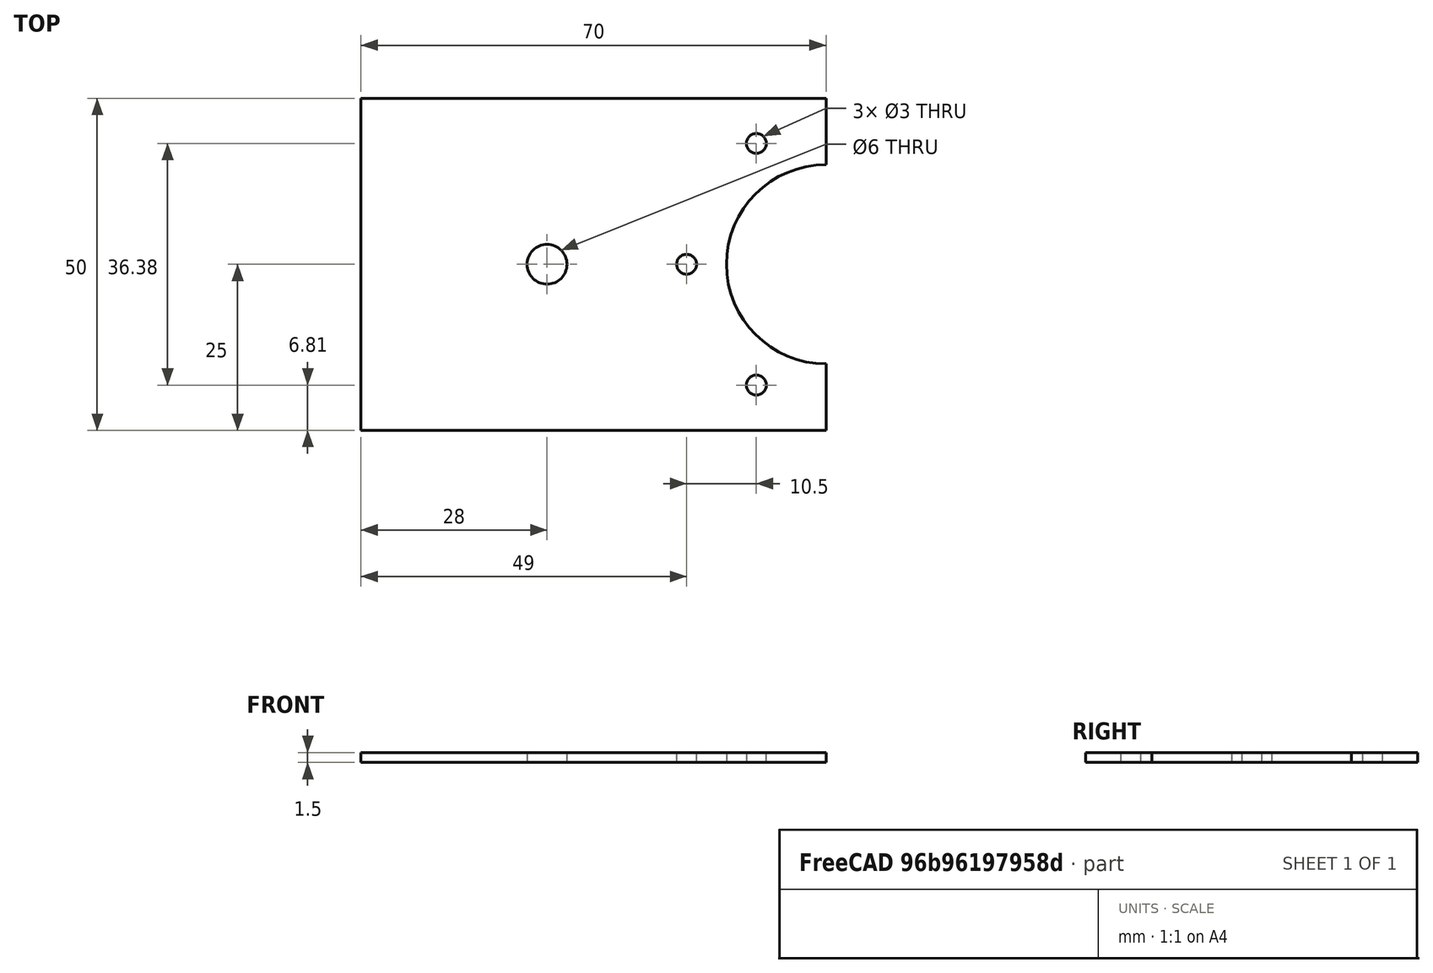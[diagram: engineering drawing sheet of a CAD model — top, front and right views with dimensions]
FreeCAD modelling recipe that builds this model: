
FCSTD DOCUMENT  (FreeCAD 0.21R33668 +26 (Git))
Label: hoja arma
License: All rights reserved
LicenseURL: https://en.wikipedia.org/wiki/All_rights_reserved
objects: TechDraw::DrawViewDimension×10, Sketcher::SketchObject×1, PartDesign::Pad×1, PartDesign::Body×1, TechDraw::DrawSVGTemplate×1, TechDraw::DrawProjGroupItem×1, TechDraw::DrawProjGroup×1, TechDraw::DrawViewAnnotation×1, TechDraw::DrawPage×1
note: 18 computed .brp shape members not serialized (recipe doc carries the construction recipe); baked Part::Feature solids carry a one-line shape summary decoded from their .brp

FEATURE [Sketcher::SketchObject] Sketch
  FullyConstrained = true
  MapMode = 5
  Support = -> [XY_Plane]
  sketch-geometry (10):
    g0: LineSegment StartX=70 StartY=0 StartZ=0 EndX=0 EndY=0 EndZ=0
    g1: LineSegment StartX=0 StartY=0 StartZ=0 EndX=0 EndY=50 EndZ=0
    g2: LineSegment StartX=0 StartY=50 StartZ=0 EndX=70 EndY=50 EndZ=0
    g3: LineSegment StartX=70 StartY=50 StartZ=0 EndX=70 EndY=40 EndZ=0
    g4: LineSegment StartX=70 StartY=0 StartZ=0 EndX=70 EndY=10 EndZ=0
    g5: ArcOfCircle CenterX=70 CenterY=25 CenterZ=0 NormalX=0 NormalY=0 NormalZ=1 AngleXU=0 Radius=15 StartAngle=1.5708 EndAngle=4.71239
    g6: Circle CenterX=28 CenterY=25 CenterZ=0 NormalX=0 NormalY=0 NormalZ=1 AngleXU=0 Radius=3
    g7: Circle CenterX=49 CenterY=25 CenterZ=0 NormalX=0 NormalY=0 NormalZ=1 AngleXU=0 Radius=1.5
    g8: Circle CenterX=59.5 CenterY=43.19 CenterZ=0 NormalX=0 NormalY=0 NormalZ=1 AngleXU=0 Radius=1.5
    g9: Circle CenterX=59.5 CenterY=6.81 CenterZ=0 NormalX=0 NormalY=0 NormalZ=1 AngleXU=0 Radius=1.5
  constraints (30):
    c: PointOnObject(g0,g-1)
    c: Coincident(g0,g-1)
    c: Coincident(g0,g1)
    c: PointOnObject(g1,g-2)
    c: Coincident(g1,g2)
    c: Horizontal(g2)
    c: DistanceY(g1,g1) = 50
    c: DistanceX(g0,g0) = 70
    c: DistanceX(g2,g2) = 70
    c: Coincident(g3,g2)
    c: Vertical(g3)
    c: Coincident(g4,g0)
    c: Vertical(g4)
    c: DistanceY(g4,g4) = 10
    c: DistanceY(g3,g3) = 10
    c: Coincident(g5,g3)
    c: Coincident(g5,g4)
    c: DistanceX(g4,g5) = 0
    c: Diameter(g6) = 6
    c: DistanceX(g0,g6) = 28
    c: DistanceY(g5,g6) = 0
    c: Diameter(g7) = 3
    c: DistanceY(g7,g5) = 0
    c: DistanceX(g7,g5) = 21
    c: DistanceX(g7,g8) = 10.5
    c: DistanceY(g7,g8) = 18.19
    c: DistanceX(g7,g9) = 10.5
    c: DistanceY(g9,g7) = 18.19
    c: Diameter(g8) = 3
    c: Diameter(g9) = 3
FEATURE [PartDesign::Pad] Pad
  Direction = (0,0,1)
  Length = 1.5
  Length2 = 10
  Profile = -> Sketch
  ReferenceAxis = -> Sketch [N_Axis]
  Type = 0
FEATURE [PartDesign::Body] Body  label="Cuerpo"
  Group = -> [Sketch,Pad]
  Origin = -> Origin
  Tip = -> Pad
FEATURE [TechDraw::DrawSVGTemplate] Template
  EditableTexts = Designed_by_Name=Enrique Gómez; Drawing_number=1; FC-Date=10/10/2023; FC-SC=2:1; FC-SH=1; FC-Title=Hoja del arma; Subtitle=Pepperoni; Weight=N/A
  Height = 210
  Orientation = 1
  Template = /snap/freecad/759/usr/share/Mod/TechDraw/Templates/A4_LandscapeTD.svg
  Width = 297
FEATURE [TechDraw::DrawProjGroupItem] ProjItem  label="Front"
  CoarseView = false
  Direction = (0,0,1)
  Focus = 100
  HardHidden = false
  IsoCount = 0
  IsoHidden = false
  IsoVisible = false
  LockPosition = true
  Perspective = false
  Rotation = 0
  RotationVector = (1,1e-06,0)
  Scale = 2
  ScaleType = 2
  ScrubCount = 0
  SeamHidden = false
  SeamVisible = false
  SmoothHidden = false
  SmoothVisible = true
  Source = -> [Body]
  Type = 0
  X = 0
  XDirection = (1,1e-06,0)
  Y = 0
FEATURE [TechDraw::DrawProjGroup] ProjGroup
  Anchor = -> ProjItem
  AutoDistribute = true
  LockPosition = false
  ProjectionType = 0
  Rotation = 0
  Scale = 2
  ScaleType = 2
  Source = -> [Body]
  Views = -> [ProjItem]
  X = 104.135
  Y = 138.929
  spacingX = 15
  spacingY = 15
FEATURE [TechDraw::DrawViewDimension] Dimension
  AngleOverride = false
  Arbitrary = false
  ArbitraryTolerances = false
  EqualTolerance = true
  ExtensionAngle = 0
  FormatSpec = %.2w
  FormatSpecOverTolerance = %+.2w
  FormatSpecUnderTolerance = %+.2w
  Inverted = false
  LineAngle = 0
  LockPosition = false
  MeasureType = 1
  OverTolerance = 0
  References2D = -> [ProjItem]
  Rotation = 0
  ScaleType = 0
  TheoreticalExact = false
  Type = 2
  UnderTolerance = 0
  X = -83.6701
  Y = -0.376252
FEATURE [TechDraw::DrawViewDimension] Dimension001
  AngleOverride = false
  Arbitrary = false
  ArbitraryTolerances = false
  EqualTolerance = true
  ExtensionAngle = 0
  FormatSpec = %.2w
  FormatSpecOverTolerance = %+.2w
  FormatSpecUnderTolerance = %+.2w
  Inverted = false
  LineAngle = 0
  LockPosition = false
  MeasureType = 1
  OverTolerance = 0
  References2D = -> [ProjItem]
  Rotation = 0
  ScaleType = 0
  TheoreticalExact = false
  Type = 1
  UnderTolerance = 0
  X = -4.80173
  Y = -64.0963
FEATURE [TechDraw::DrawViewDimension] Dimension002
  AngleOverride = false
  Arbitrary = false
  ArbitraryTolerances = false
  EqualTolerance = true
  ExtensionAngle = 0
  FormatSpec = ⌀%.2w
  FormatSpecOverTolerance = %+.2w
  FormatSpecUnderTolerance = %+.2w
  Inverted = false
  LineAngle = 0
  LockPosition = false
  MeasureType = 1
  OverTolerance = 0
  References2D = -> [ProjItem]
  Rotation = 0
  ScaleType = 0
  TheoreticalExact = false
  Type = 5
  UnderTolerance = 0
  X = -32.8764
  Y = -3.71677
FEATURE [TechDraw::DrawViewDimension] Dimension003
  AngleOverride = false
  Arbitrary = false
  ArbitraryTolerances = false
  EqualTolerance = true
  ExtensionAngle = 0
  FormatSpec = ⌀%.2w
  FormatSpecOverTolerance = %+.2w
  FormatSpecUnderTolerance = %+.2w
  Inverted = false
  LineAngle = 0
  LockPosition = false
  MeasureType = 1
  OverTolerance = 0
  References2D = -> [ProjItem]
  Rotation = 0
  ScaleType = 0
  TheoreticalExact = false
  Type = 5
  UnderTolerance = 0
  X = 4.26946
  Y = -6.57343
FEATURE [TechDraw::DrawViewDimension] Dimension004
  AngleOverride = false
  Arbitrary = false
  ArbitraryTolerances = false
  EqualTolerance = true
  ExtensionAngle = 0
  FormatSpec = R%.2w
  FormatSpecOverTolerance = %+.2w
  FormatSpecUnderTolerance = %+.2w
  Inverted = false
  LineAngle = 0
  LockPosition = false
  MeasureType = 1
  OverTolerance = 0
  References2D = -> [ProjItem]
  Rotation = 0
  ScaleType = 0
  TheoreticalExact = false
  Type = 4
  UnderTolerance = 0
  X = 54.8136
  Y = -1.79481
FEATURE [TechDraw::DrawViewDimension] Dimension005
  AngleOverride = false
  Arbitrary = false
  ArbitraryTolerances = false
  EqualTolerance = true
  ExtensionAngle = 0
  FormatSpec = %.2w
  FormatSpecOverTolerance = %+.2w
  FormatSpecUnderTolerance = %+.2w
  Inverted = false
  LineAngle = 0
  LockPosition = false
  MeasureType = 1
  OverTolerance = 0
  References2D = -> [ProjItem]
  Rotation = 0
  ScaleType = 0
  TheoreticalExact = false
  Type = 2
  UnderTolerance = 0
  X = 83.9793
  Y = -37.4718
FEATURE [TechDraw::DrawViewDimension] Dimension008
  AngleOverride = false
  Arbitrary = false
  ArbitraryTolerances = false
  EqualTolerance = true
  ExtensionAngle = 0
  FormatSpec = %.2w
  FormatSpecOverTolerance = %+.2w
  FormatSpecUnderTolerance = %+.2w
  Inverted = false
  LineAngle = 0
  LockPosition = false
  MeasureType = 1
  OverTolerance = 0
  References2D = -> [ProjItem]
  Rotation = 0
  ScaleType = 0
  TheoreticalExact = false
  Type = 1
  UnderTolerance = 0
  X = -44.7526
  Y = -53.301
FEATURE [TechDraw::DrawViewDimension] Dimension009
  AngleOverride = false
  Arbitrary = false
  ArbitraryTolerances = false
  EqualTolerance = true
  ExtensionAngle = 0
  FormatSpec = %.2w
  FormatSpecOverTolerance = %+.2w
  FormatSpecUnderTolerance = %+.2w
  Inverted = false
  LineAngle = 0
  LockPosition = false
  MeasureType = 1
  OverTolerance = 0
  References2D = -> [ProjItem]
  Rotation = 0
  ScaleType = 0
  TheoreticalExact = false
  Type = 1
  UnderTolerance = 0
  X = 3.52311
  Y = -53.3456
FEATURE [TechDraw::DrawViewDimension] Dimension010
  AngleOverride = false
  Arbitrary = false
  ArbitraryTolerances = false
  EqualTolerance = true
  ExtensionAngle = 0
  FormatSpec = %.2w
  FormatSpecOverTolerance = %+.2w
  FormatSpecUnderTolerance = %+.2w
  Inverted = false
  LineAngle = 0
  LockPosition = false
  MeasureType = 1
  OverTolerance = 0
  References2D = -> [ProjItem]
  Rotation = 0
  ScaleType = 0
  TheoreticalExact = false
  Type = 1
  UnderTolerance = 0
  X = 37.9205
  Y = -53.3564
FEATURE [TechDraw::DrawViewDimension] Dimension011
  AngleOverride = false
  Arbitrary = false
  ArbitraryTolerances = false
  EqualTolerance = true
  ExtensionAngle = 0
  FormatSpec = %.2w
  FormatSpecOverTolerance = %+.2w
  FormatSpecUnderTolerance = %+.2w
  Inverted = false
  LineAngle = 0
  LockPosition = false
  MeasureType = 1
  OverTolerance = 0
  References2D = -> [ProjItem]
  Rotation = 0
  ScaleType = 0
  TheoreticalExact = false
  Type = 2
  UnderTolerance = 0
  X = 14.7322
  Y = 18.9923
FEATURE [TechDraw::DrawViewAnnotation] Annotation
  Font = osifont
  LineSpace = 100
  LockPosition = false
  MaxWidth = -1
  Rotation = 0
  ScaleType = 0
  Text = Unidades en mm
  TextSize = 5
  TextStyle = 0
  X = 210.321
  Y = 34.1823
FEATURE [TechDraw::DrawPage] Page
  KeepUpdated = true
  NextBalloonIndex = 1
  ProjectionType = 0
  Template = -> Template
  Views = -> [ProjGroup,Dimension,Dimension001,Dimension002,Dimension003,Dimension004,Dimension005,Dimension008,Dimension009,Dimension010,Dimension011,Annotation]
